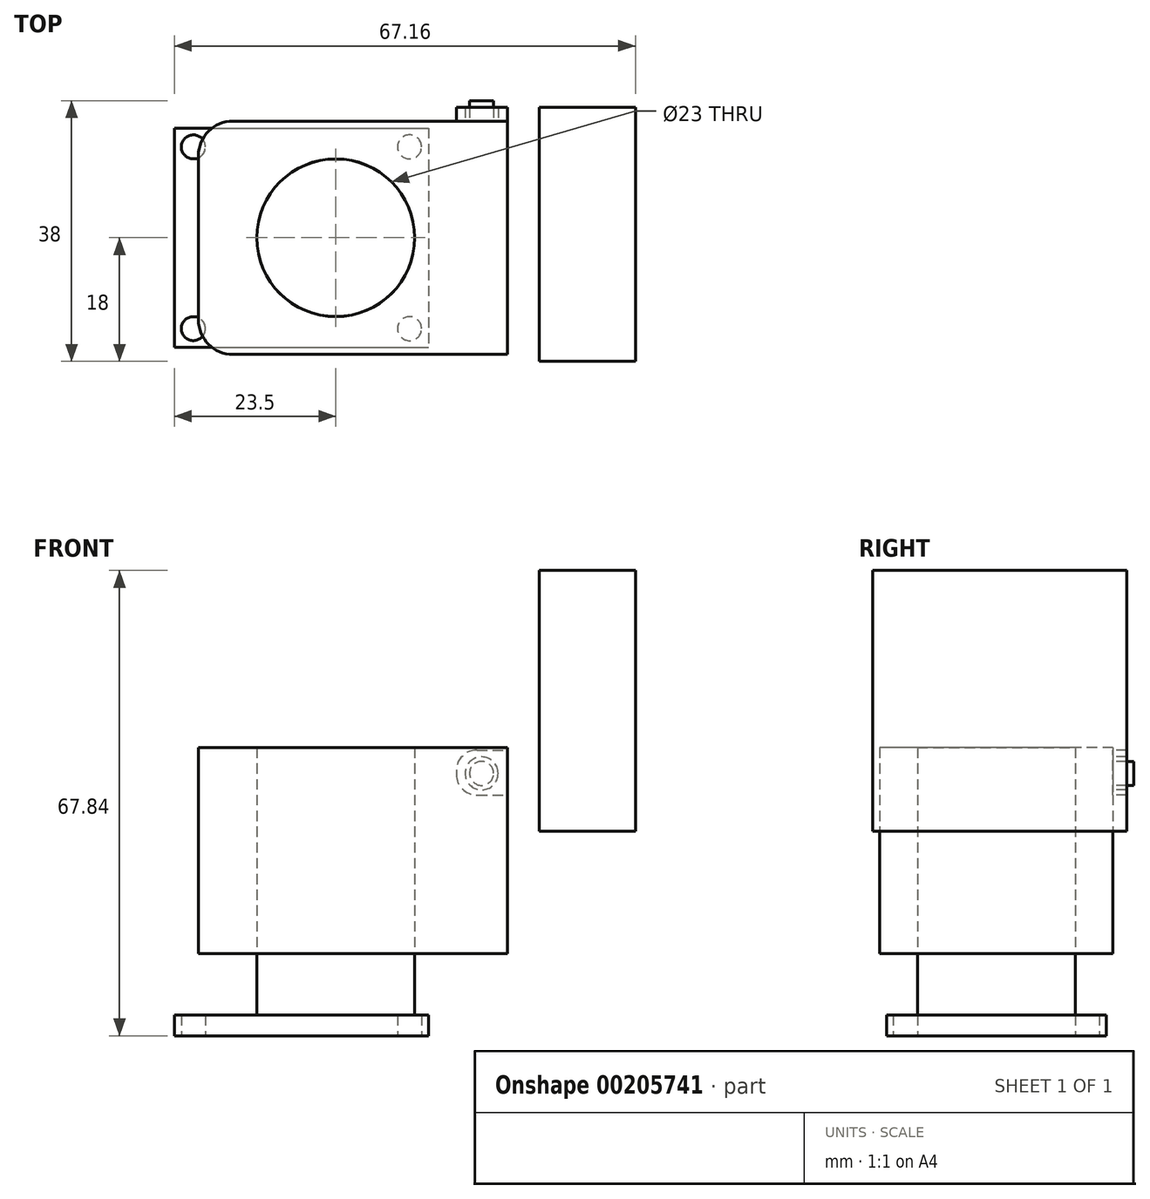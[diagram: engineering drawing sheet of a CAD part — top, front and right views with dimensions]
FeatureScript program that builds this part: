
annotation { "Feature Type Name" : "Feature", "Feature Type Description" : "" }
export const myFeature = defineFeature(function(context is Context, id is Id, definition is map)
    precondition{}
    {
        {
            var Q0;
            Q0=qCreatedBy(makeId("Top.planeOp"),FACE);
            var sketch = newSketch(context, id + "F0", { "sketchPlane" : qUnion([Q0])});
            skLineSegment(sketch, "E0.bottom", {"start": v(-18.5, 16) * mm, "end": v(18.5, 16) * mm});
            skLineSegment(sketch, "E0.top", {"start": v(-18.5, -16) * mm, "end": v(18.5, -16) * mm});
            skLineSegment(sketch, "E0.left", {"start": v(-18.5, 16) * mm, "end": v(-18.5, -16) * mm});
            skLineSegment(sketch, "E0.right", {"start": v(18.5, 16) * mm, "end": v(18.5, -16) * mm});
            skPoint(sketch, "E0.middle", {"position": v(0, 0) * mm});
            skCircle(sketch, "E1", {"center": v(-15.75, 13.25) * mm, "radius": 1.75 * mm});
            skLineSegment(sketch, "E2", {"start": v(0, 16) * mm, "end": v(0, -16) * mm, "construction": true});
            skLineSegment(sketch, "E3", {"start": v(18.5, 0) * mm, "end": v(-18.5, 0) * mm, "construction": true});
            skCircle(sketch, "E4.MirrorC", {"center": v(15.75, 13.25) * mm, "radius": 1.75 * mm});
            skCircle(sketch, "E5.MirrorC", {"center": v(15.75, -13.25) * mm, "radius": 1.75 * mm});
            skCircle(sketch, "E6.MirrorC", {"center": v(-15.75, -13.25) * mm, "radius": 1.75 * mm});
            skCircle(sketch, "E7", {"center": v(5, 0) * mm, "radius": 11.5 * mm});
            skLineSegment(sketch, "E8", {"start": v(-14, 13.25) * mm, "end": v(-17.5, 13.25) * mm, "construction": true});
            skLineSegment(sketch, "E9", {"start": v(-15.75, 15) * mm, "end": v(-15.75, 11.5) * mm, "construction": true});
            skSolve(sketch);
        }
        {
            var Q0;
            Q0=makeQuery(id+"F0.imprint","IMPRINT",FACE,{"disambiguationData":[TD([[makeQuery(id+"F0.imprint","IMPRINT",EDGE,{"derivedFrom":sQuery(id+"F0.wireOp",EDGE,"E0.bottom")}),-1.0]])]});
            extrude(context, id + "F1", {"entities" : qUnion([Q0]), "depth" : 3 * mm});
        }
        {
            var Q0;
            Q0=makeQuery(id+"F0.imprint","IMPRINT",FACE,{"disambiguationData":[TD([[makeQuery(id+"F0.imprint","IMPRINT",EDGE,{"derivedFrom":sQuery(id+"F0.wireOp",EDGE,"E7")}),1.0]])]});
            extrude(context, id + "F2", {"entities" : qUnion([Q0]), "operationType" : NewBodyOperationType.ADD, "depth" : 12 * mm});
        }
        {
            var Q0;
            Q0=makeQuery(id+"F2.opExtrude","CAP_FACE",FACE,{"disambiguationData":[OSD([sQuery(id+"F0.wireOp",EDGE,"E7")])],"isStart":false});
            var sketch = newSketch(context, id + "F3", { "sketchPlane" : qUnion([Q0])});
            skCircle(sketch, "E10", {"center": v(5, 0) * mm, "radius": 11.5 * mm});
            skLineSegment(sketch, "E11.bottom", {"start": v(-15, 17) * mm, "end": v(30, 17) * mm});
            skLineSegment(sketch, "E11.top", {"start": v(-15, -17) * mm, "end": v(30, -17) * mm});
            skLineSegment(sketch, "E11.left", {"start": v(-15, 17) * mm, "end": v(-15, -17) * mm});
            skLineSegment(sketch, "E11.right", {"start": v(30, 17) * mm, "end": v(30, -17) * mm});
            skPoint(sketch, "E11.middle", {"position": v(7.5, 0) * mm});
            skLineSegment(sketch, "E12", {"start": v(5, 11.5) * mm, "end": v(5, -11.5) * mm, "construction": true});
            skLineSegment(sketch, "E13", {"start": v(7.5, 17) * mm, "end": v(7.5, -17) * mm, "construction": true});
            skSolve(sketch);
        }
        {
            var Q0;
            Q0=makeQuery(id+"F3.imprint","IMPRINT",FACE,{"disambiguationData":[TD([[makeQuery(id+"F3.imprint","IMPRINT",EDGE,{"derivedFrom":sQuery(id+"F3.wireOp",EDGE,"E10")}),1.0]])]});
            extrude(context, id + "F4", {"entities" : qUnion([Q0]), "operationType" : NewBodyOperationType.REMOVE, "depth" : 2 * mm});
        }
        {
            var Q0;
            Q0=makeQuery(id+"F3.imprint","IMPRINT",FACE,{"disambiguationData":[TD([[makeQuery(id+"F3.imprint","IMPRINT",EDGE,{"derivedFrom":sQuery(id+"F3.wireOp",EDGE,"E11.bottom")}),-1.0]])]});
            var Q1;
            Q1=makeQuery(id+"F3.imprint","IMPRINT",FACE,{"disambiguationData":[TD([[makeQuery(id+"F3.imprint","IMPRINT",EDGE,{"derivedFrom":sQuery(id+"F3.wireOp",EDGE,"E10")}),1.0]])]});
            extrude(context, id + "F5", {"entities" : qUnion([Q0, Q1]), "depth" : 30 * mm});
        }
        {
            var Q0;
            Q0=makeQuery(id+"F5.opExtrude","SWEPT_FACE",FACE,{"disambiguationData":[OSD([sQuery(id+"F3.wireOp",EDGE,"E11.bottom")])]});
            var sketch = newSketch(context, id + "F6", { "sketchPlane" : qUnion([Q0])});
            skCircle(sketch, "E14", {"center": v(-26.25, 38.25) * mm, "radius": 1.75 * mm});
            skSolve(sketch);
        }
        {
            var Q0;
            Q0=makeQuery(id+"F6.imprint","IMPRINT",FACE,{"disambiguationData":[TD([[makeQuery(id+"F6.imprint","IMPRINT",EDGE,{"derivedFrom":sQuery(id+"F6.wireOp",EDGE,"E14")}),1.0]])]});
            extrude(context, id + "F7", {"entities" : qUnion([Q0]), "operationType" : NewBodyOperationType.ADD, "depth" : 3 * mm});
        }
        {
            var Q0;
            Q0=makeQuery(id+"F5.opExtrude","SWEPT_FACE",FACE,{"disambiguationData":[OSD([sQuery(id+"F3.wireOp",EDGE,"E11.bottom")])]});
            var sketch = newSketch(context, id + "F8", { "sketchPlane" : qUnion([Q0])});
            skCircle(sketch, "E15", {"center": v(-26.25, 38.25) * mm, "radius": 2.4 * mm});
            skLineSegment(sketch, "E16.bottom", {"start": v(-25.57, 41.65) * mm, "end": v(-34.66, 41.65) * mm});
            skLineSegment(sketch, "E16.top", {"start": v(-25.57, 35.08) * mm, "end": v(-34.66, 35.08) * mm});
            skLineSegment(sketch, "E16.left", {"start": v(-22.57, 38.65) * mm, "end": v(-22.57, 38.08) * mm});
            skLineSegment(sketch, "E16.right", {"start": v(-34.66, 41.65) * mm, "end": v(-34.66, 35.08) * mm});
            skPoint(sketch, "E17.visualSharp", {"position": v(-22.57, 41.65) * mm});
            skArc(sketch, "E17.filletArc", {"start": v(-22.57, 38.65) * mm, "mid": v(-23.45, 40.77) * mm, "end": v(-25.57, 41.65) * mm});
            skPoint(sketch, "E18.visualSharp", {"position": v(-22.57, 35.08) * mm});
            skArc(sketch, "E18.filletArc", {"start": v(-25.57, 35.08) * mm, "mid": v(-23.45, 35.96) * mm, "end": v(-22.57, 38.08) * mm});
            skLineSegment(sketch, "E19.bottom", {"start": v(-34.66, 29.84) * mm, "end": v(-48.66, 29.84) * mm});
            skLineSegment(sketch, "E19.top", {"start": v(-34.66, 67.84) * mm, "end": v(-48.66, 67.84) * mm});
            skLineSegment(sketch, "E19.left", {"start": v(-34.66, 29.84) * mm, "end": v(-34.66, 67.84) * mm});
            skLineSegment(sketch, "E19.right", {"start": v(-48.66, 29.84) * mm, "end": v(-48.66, 67.84) * mm});
            skSolve(sketch);
        }
        {
            var Q0;
            Q0=makeQuery(id+"F8.imprint","IMPRINT",FACE,{"disambiguationData":[TD([[makeQuery(id+"F8.imprint","IMPRINT",EDGE,{"derivedFrom":sQuery(id+"F8.wireOp",EDGE,"E15")}),-1.0]])]});
            var Q1;
            {var subQ0=sQuery(id+"F8.wireOp",EDGE,"E19.left");var subQ1=sQuery(id+"F8.wireOp",EDGE,"E16.bottom");var subQ2=makeQuery(id+"F8.imprint","INTERSECT",VERTEX,{"derivedFrom":[subQ1,subQ0]});Q1=makeQuery(id+"F8.imprint","IMPRINT",FACE,{"disambiguationData":[TD([[makeQuery(id+"F8.imprint","IMPRINT",EDGE,{"disambiguationData":[TD([[subQ2,1.0]])],"derivedFrom":subQ0}),-1.0]])]});}
            extrude(context, id + "F9", {"entities" : qUnion([Q0, Q1]), "depth" : 2 * mm});
        }
        {
            var Q0;
            {var subQ3=sQuery(id+"F8.wireOp",EDGE,"E19.bottom");Q0=makeQuery(id+"F8.imprint","IMPRINT",FACE,{"disambiguationData":[TD([[makeQuery(id+"F8.imprint","IMPRINT",EDGE,{"derivedFrom":subQ3}),-1.0]])]});}
            extrude(context, id + "F10", {"entities" : qUnion([Q0]), "operationType" : NewBodyOperationType.ADD, "oppositeDirection" : true, "depth" : 35 * mm, "hasSecondDirection" : true, "secondDirectionOppositeDirection" : false, "secondDirectionDepth" : 2 * mm});
        }
        {
            var Q0;
            Q0=makeQuery(id+"F5.opExtrude","SWEPT_EDGE",EDGE,{"disambiguationData":[OSD([sQuery(id+"F3.wireOp",EDGE,"E11.top"),sQuery(id+"F3.wireOp",EDGE,"E11.left")])]});
            var Q1;
            Q1=makeQuery(id+"F5.opExtrude","SWEPT_EDGE",EDGE,{"disambiguationData":[OSD([sQuery(id+"F3.wireOp",EDGE,"E11.bottom"),sQuery(id+"F3.wireOp",EDGE,"E11.left")])]});
            fillet(context, id + "F11", {"entities" : qUnion([Q0, Q1]), "radius" : 5 * mm, "tangentPropagation" : true, "allowEdgeOverflow" : false});
        }
    });
